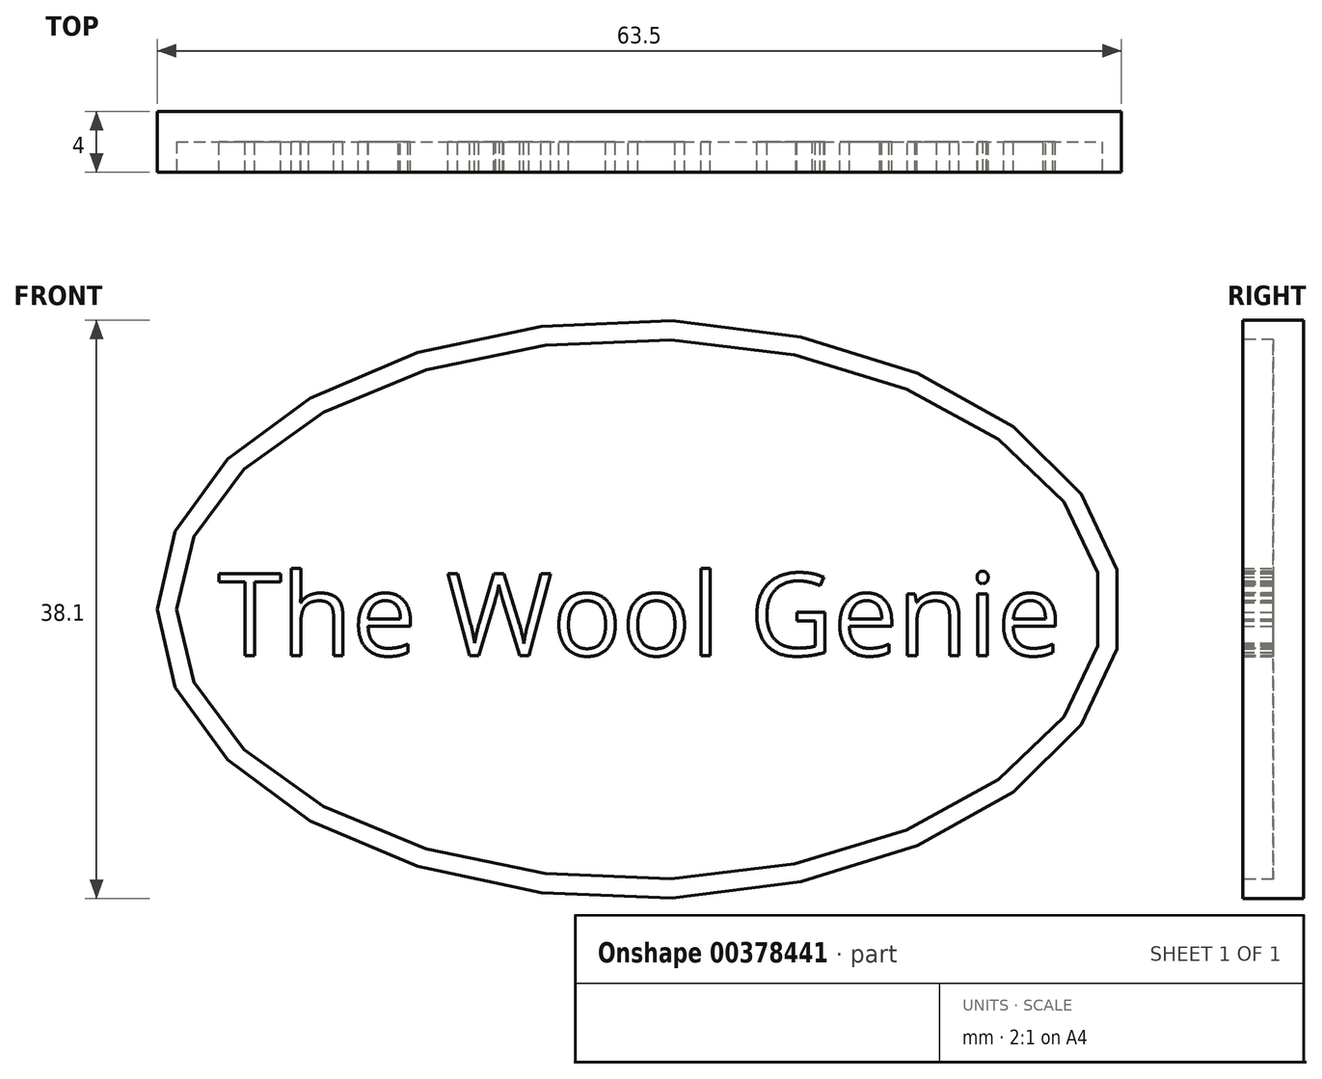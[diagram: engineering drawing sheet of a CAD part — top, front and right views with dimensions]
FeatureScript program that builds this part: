
annotation { "Feature Type Name" : "Feature", "Feature Type Description" : "" }
export const myFeature = defineFeature(function(context is Context, id is Id, definition is map)
    precondition{}
    {
        {
            var Q0;
            Q0=qCreatedBy(makeId("Front.planeOp"),FACE);
            var sketch = newSketch(context, id + "F0", { "sketchPlane" : qUnion([Q0])});
            skEllipse(sketch, "E0", {"center": v(0, 0) * mm, "majorRadius": 31.75 * mm, "minorRadius": 19.05 * mm, "majorAxis": v(-1, 0)});
            skSolve(sketch);
        }
        {
            var Q0;
            Q0=makeQuery(id+"F0.imprint","IMPRINT",FACE,{"disambiguationData":[TD([[makeQuery(id+"F0.imprint","IMPRINT",EDGE,{"derivedFrom":sQuery(id+"F0.wireOp",EDGE,"E0")}),1.0]])]});
            extrude(context, id + "F1", {"entities" : qUnion([Q0]), "depth" : 4 * mm});
        }
        {
            var Q0;
            Q0=makeQuery(id+"F1.opExtrude","CAP_FACE",FACE,{"disambiguationData":[OSD([sQuery(id+"F0.wireOp",EDGE,"E0")])],"isStart":false});
            var sketch = newSketch(context, id + "F2", { "sketchPlane" : qUnion([Q0])});
            skEllipse(sketch, "E1", {"center": v(0, 0) * mm, "majorRadius": 30.48 * mm, "minorRadius": 17.78 * mm, "majorAxis": v(-1, 0)});
            skSolve(sketch);
        }
        {
            var Q0;
            Q0=makeQuery(id+"F2.imprint","IMPRINT",FACE,{"disambiguationData":[TD([[makeQuery(id+"F2.imprint","IMPRINT",EDGE,{"derivedFrom":sQuery(id+"F2.wireOp",EDGE,"E1")}),1.0]])]});
            extrude(context, id + "F3", {"entities" : qUnion([Q0]), "operationType" : NewBodyOperationType.REMOVE, "oppositeDirection" : true, "depth" : 2 * mm});
        }
        {
            var Q0;
            Q0=makeQuery(id+"F3.boolean.opBoolean","COPY",FACE,{"derivedFrom":makeQuery(id+"F3.opExtrude","CAP_FACE",FACE,{"disambiguationData":[OSD([sQuery(id+"F2.wireOp",EDGE,"E1")])],"isStart":false})});
            var sketch = newSketch(context, id + "F4", { "sketchPlane" : qUnion([Q0])});
            skText(sketch, "E2", { "text": "The Wool Genie", "fontName": "OpenSans-Regular.ttf"});
            const initialGuessF4  = {"E2": [-0.02774, -0.00303, 1, 0, 0.00544]};
            skSetInitialGuess(sketch, initialGuessF4);
            skSolve(sketch);
        }
        {
            var Q0;
            Q0=qSketchRegion(id+"F4",true);
            extrude(context, id + "F5", {"entities" : qUnion([Q0]), "operationType" : NewBodyOperationType.ADD, "depth" : 2 * mm});
        }
    });
